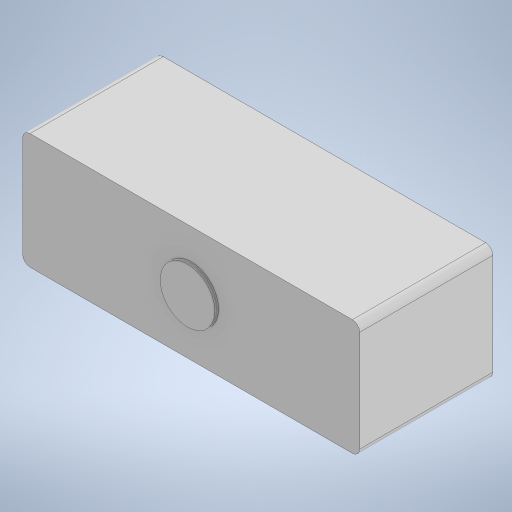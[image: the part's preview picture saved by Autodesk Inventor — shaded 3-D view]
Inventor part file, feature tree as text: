
AUTODESK INVENTOR PART (.ipt)
format: ipt  version: 2024.3 (Build 283343010, 343A)  size: 198,656 bytes
history: native  units: mm
features: sketch x3, extrude x2, fillet x1, hole x1
ambient origin geometry x8: Origin, YZ Plane, XZ Plane, XY Plane, X Axis, Y Axis, Z Axis, Center Point
bodies: Body1 (feature_tree)
feature tree (7):
  extrude  "押し出し2"  Depth=92.3mm
  fillet  "フィレット1"  Radius=31.7mm
  hole  "穴1"  [1 undecoded]
  extrude  "押し出し3"  Depth=2.0mm
  sketch  "スケッチ2"
  sketch  "スケッチ3"
  sketch  "スケッチ4"
note: 1 required parameter value undecoded (feature->parameter linkage not recoverable at this tier; creation-order binding heuristic only, values carry confidence <= 0.55)
